FCSTD DOCUMENT  (FreeCAD 0.18.3R)
Label: test_world
License: All rights reserved
LicenseURL: http://en.wikipedia.org/wiki/All_rights_reserved
objects: Part::Part2DObjectPython×13, App::DocumentObjectGroup×6
note: 13 computed .brp shape members not serialized (recipe doc carries the construction recipe); baked Part::Feature solids carry a one-line shape summary decoded from their .brp

FEATURE [Part::Part2DObjectPython] Wire  # Draft 2D object (typed FeaturePython)
  ChamferSize = 0
  Closed = false
  End = (10000,4000,0)
  FilletRadius = 0
  Length = 57122.2
  MakeFace = true
  Placement = pos=(0,4000,0) rot=(0,0,1;0rad)
  Points = (27) [(0,0,0),(-5000,0,0),(-5000,-1000,0),(-4000,-1000,0),(-4000,-6000,0),(-3000,-7000,0),(-2000,-7000,0),(-2000,-8000,0),(-1800.78,-8000,0),+18 more]
  Start = (0,4000,0)
  Subdivisions = 0
FEATURE [Part::Part2DObjectPython] Wire001  # Draft 2D object (typed FeaturePython)
  ChamferSize = 0
  Closed = true
  End = (10000,4000,0)
  FilletRadius = 0
  Length = 67122.2
  MakeFace = true
  Placement = pos=(0,4000,0) rot=(0,0,1;0rad)
  Points = (27) [(0,0,0),(-5000,0,0),(-5000,-1000,0),(-4000,-1000,0),(-4000,-6000,0),(-3000,-7000,0),(-2000,-7000,0),(-2000,-8000,0),(-1800.78,-8000,0),+18 more]
  Start = (0,4000,0)
  Subdivisions = 0
FEATURE [App::DocumentObjectGroup] Group001  label="free_space"
  Group = -> [Wire001]
FEATURE [Part::Part2DObjectPython] Wire002  # Draft 2D object (typed FeaturePython)
  ChamferSize = 0
  Closed = true
  End = (10000,4000,0)
  FilletRadius = 0
  Length = 67122.2
  MakeFace = true
  Placement = pos=(0,4000,0) rot=(0,0,1;0rad)
  Points = (27) [(0,0,0),(-5000,0,0),(-5000,-1000,0),(-4000,-1000,0),(-4000,-6000,0),(-3000,-7000,0),(-2000,-7000,0),(-2000,-8000,0),(-1800.78,-8000,0),+18 more]
  Start = (0,4000,0)
  Subdivisions = 0
FEATURE [App::DocumentObjectGroup] Group002  label="drivable_zone"
  Group = -> [Wire002]
FEATURE [Part::Part2DObjectPython] Wire003  # Draft 2D object (typed FeaturePython)
  ChamferSize = 0
  Closed = true
  End = (5000,2000,0)
  FilletRadius = 0
  Length = 10000
  MakeFace = true
  Placement = pos=(1000,2000,0) rot=(0,0,1;0rad)
  Points = (4) [(0,0,0),(0,-1000,0),(4000,-1000,0),(4000,0,0)]
  Start = (1000,2000,0)
  Subdivisions = 0
FEATURE [App::DocumentObjectGroup] Group003  label="avoid_zone"
  Group = -> [Wire003]
FEATURE [Part::Part2DObjectPython] Wire004  # Draft 2D object (typed FeaturePython)
  ChamferSize = 0
  Closed = true
  End = (11000,-4000,0)
  FilletRadius = 0
  Length = 32000
  MakeFace = true
  Placement = pos=(11000,-3000,0) rot=(0,0,1;0rad)
  Points = (4) [(0,0,0),(-15000,0,0),(-15000,-1000,0),(0,-1000,0)]
  Start = (11000,-3000,0)
  Subdivisions = 0
FEATURE [App::DocumentObjectGroup] Group004  label="exclusion_zone"
  Group = -> [Wire004]
FEATURE [Part::Part2DObjectPython] Circle  # Draft 2D object (typed FeaturePython)
  FirstAngle = 0
  LastAngle = 0
  MakeFace = true
  Placement = pos=(-3820.77,3098.08,0) rot=(0,0,1;0rad)
  Radius = 70
FEATURE [Part::Part2DObjectPython] Circle001  # Draft 2D object (typed FeaturePython)
  FirstAngle = 0
  LastAngle = 0
  MakeFace = true
  Placement = pos=(-28.5351,3607.21,0) rot=(0,0,1;0rad)
  Radius = 70
FEATURE [Part::Part2DObjectPython] Circle002  # Draft 2D object (typed FeaturePython)
  FirstAngle = 0
  LastAngle = 0
  MakeFace = true
  Placement = pos=(994.377,3607.21,0) rot=(0,0,1;0rad)
  Radius = 70
FEATURE [Part::Part2DObjectPython] Circle003  # Draft 2D object (typed FeaturePython)
  FirstAngle = 0
  LastAngle = 0
  MakeFace = true
  Placement = pos=(9792.6,-103.64,0) rot=(0,0,1;0rad)
  Radius = 70
FEATURE [Part::Part2DObjectPython] Circle004  # Draft 2D object (typed FeaturePython)
  FirstAngle = 0
  LastAngle = 0
  MakeFace = true
  Placement = pos=(7956.71,-2718.6,0) rot=(0,0,1;0rad)
  Radius = 70
FEATURE [Part::Part2DObjectPython] Circle005  # Draft 2D object (typed FeaturePython)
  FirstAngle = 0
  LastAngle = 0
  MakeFace = true
  Placement = pos=(-2783.07,-2729.45,0) rot=(0,0,1;0rad)
  Radius = 70
FEATURE [Part::Part2DObjectPython] Circle006  # Draft 2D object (typed FeaturePython)
  FirstAngle = 0
  LastAngle = 0
  MakeFace = true
  Placement = pos=(7025.73,-2718.6,0) rot=(0,0,1;0rad)
  Radius = 70
FEATURE [App::DocumentObjectGroup] Group005  label="poles"
  Group = -> [Circle,Circle001,Circle002,Circle003,Circle004,Circle005,Circle006]
FEATURE [Part::Part2DObjectPython] Rectangle  # Draft 2D object (typed FeaturePython)
  ChamferSize = 0
  Columns = 1
  FilletRadius = 0
  Height = 138.192
  Length = 1003.71
  MakeFace = true
  Placement = pos=(4.11889,3860.81,0) rot=(0,0,1;0rad)
  Rows = 1
FEATURE [App::DocumentObjectGroup] Group  label="walls"
  Group = -> [Wire,Rectangle]
